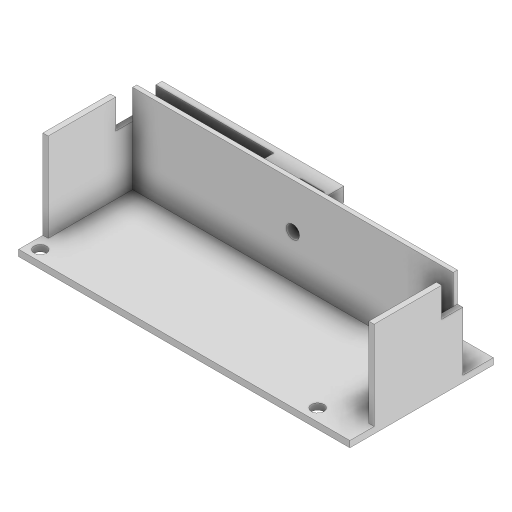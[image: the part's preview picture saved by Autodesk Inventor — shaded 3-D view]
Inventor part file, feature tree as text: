
AUTODESK INVENTOR PART (.ipt)
format: ipt  version: 2023.3 (Build 273359000, 359)  size: 321,536 bytes
history: native  units: mm
features: extrude x13, sketch x11, projected_geometry x2, fillet x1, chamfer x1, loft x1, mirror x1, plane x1
ambient origin geometry x8: Origin, YZ Plane, XZ Plane, XY Plane, X Axis, Y Axis, Z Axis, Center Point
bodies: Solid1 (feature_tree)
feature tree (31):
  extrude  "Extrusion1"  Depth=22.5mm
  sketch  "Sketch2"  dims[d2=1.5mm d3=33.0mm d4=0.0mm]
  extrude  "Extrusion2"  Depth=1.5mm TaperAngle=0.0deg
  extrude  "Extrusion3"  Depth=4.25mm
  extrude  "Extrusion4"  Depth=1.5mm
  extrude  "Extrusion5"  Depth=1.5mm
  sketch  "Sketch4"  dims[d7=1.5mm d8=1.5mm]
  extrude  "Extrusion6"  Depth=1.0mm
  extrude  "Extrusion7"  Depth=7.65mm
  fillet  "Fillet1"  Radius=2.65mm
  extrude  "Extrusion8"  Depth=17.5mm TaperAngle=0.0deg
  chamfer  "Chamfer1"  Distance=21.0mm
  extrude  "Extrusion9"  Depth=17.5mm
  loft  "Loft1"
  extrude  "Extrusion10"  Depth=3.0mm
  mirror  "Mirror1"
  extrude  "Extrusion11"  Depth=10.0mm TaperAngle=0.0deg
  plane  "Work Plane1"
  extrude  "Extrusion12"  Depth=3.0mm
  extrude  "Extrusion13"  Depth=10.0mm TaperAngle=0.0deg
  sketch  "Sketch1"  dims[d0=22.5mm d1=78.5mm]
  sketch  "Sketch3"  dims[d5=28.0mm d6=4.25mm]
  projected_geometry  "Projected Loop1"
  sketch  "Sketch6"  dims[d9=1.5mm d10=20.0mm]
  sketch  "Sketch7"  dims[d11=76.0mm d12=1.0mm]
  sketch  "Sketch8"  dims[d13=4.65mm d14=7.65mm d16=2.65mm]
  sketch  "Sketch9"  dims[d17=5.65mm d18=17.5mm d19=0.0mm d20=21.0mm d21=0.0mm]
  sketch  "Sketch10"  dims[d22=17.5mm d23=0.0mm d24=75.7mm]
  sketch  "Sketch11"  dims[d25=20.7mm d28=3.15mm]
  projected_geometry  "Projected Loop2"
  sketch  "Sketch12"  dims[d29=7.0mm d30=0.0mm d31=5.5mm d32=10.0mm d33=0.0mm d34=3.15mm d35=10.0mm d36=0.0mm d37=10.35mm d38=2.0mm d43=5.0mm d44=11.85mm d45=39.25mm d46=3.0mm d47=0.0mm d49=3.0mm d50=2.0mm d51=45.0deg d52=1.0mm d53=21.0mm d54=0.0mm d55=4.0mm d56=3.0mm d57=5.0mm d58=5.0mm d59=3.0mm d60=2.0mm d61=0.0mm d62=90.0deg d63=0.0mm d64=90.0deg d65=7.0mm d66=5.0mm d67=0.0mm d68=5.0mm d69=0.0mm d73=135.0deg d74=45.0deg d75=3.0mm d76=0.5mm d77=3.0mm d78=0.0mm d79=3.0mm d80=2.5mm d81=2.62mm d82=3.0mm d83=2.875mm d84=10.5mm d85=3.0mm d86=0.0mm]
